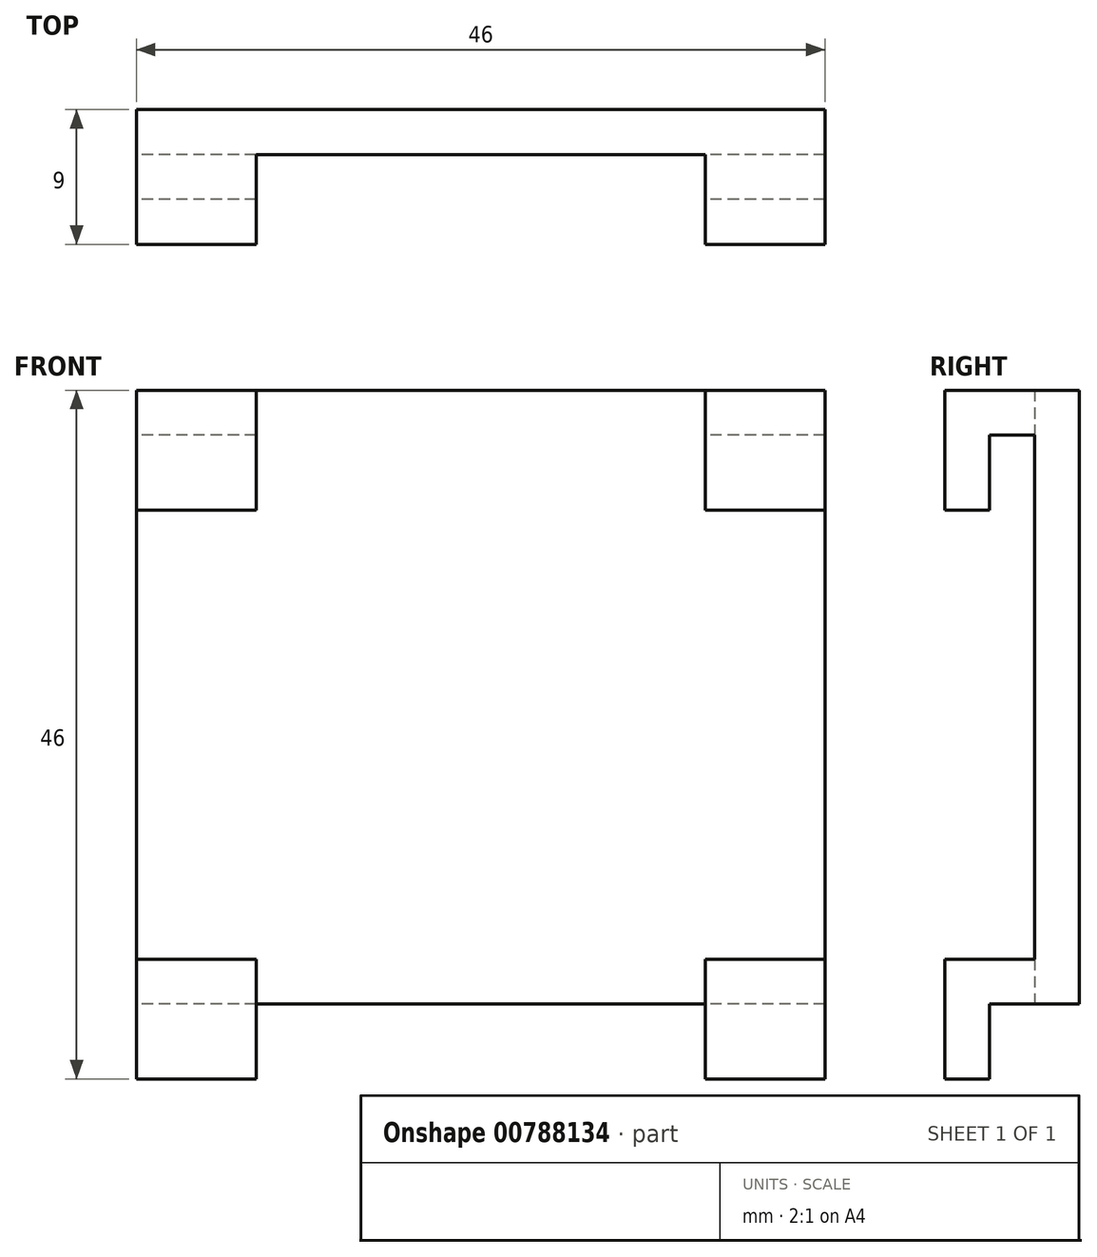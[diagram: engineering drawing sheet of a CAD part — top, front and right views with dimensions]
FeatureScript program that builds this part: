
annotation { "Feature Type Name" : "Feature", "Feature Type Description" : "" }
export const myFeature = defineFeature(function(context is Context, id is Id, definition is map)
    precondition{}
    {
        {
            var Q0;
            Q0=qCreatedBy(makeId("Front.planeOp"),FACE);
            cPlane(context, id + "F0", {"entities" : qUnion([Q0]), "cplaneType" : CPlaneType.OFFSET, "offset" : 3 * mm, "width" : 152.4 * mm, "height" : 152.4 * mm});
        }
        {
            var Q0;
            Q0=qCreatedBy(makeId("Right.planeOp"),FACE);
            var sketch = newSketch(context, id + "F1", { "sketchPlane" : qUnion([Q0])});
            skLineSegment(sketch, "E0", {"start": v(-6, 38) * mm, "end": v(-6, 3) * mm});
            skLineSegment(sketch, "E1", {"start": v(-6, 3) * mm, "end": v(-12, 3) * mm});
            skLineSegment(sketch, "E2", {"start": v(-12, 3) * mm, "end": v(-12, -5) * mm});
            skLineSegment(sketch, "E3", {"start": v(-12, -5) * mm, "end": v(-9, -5) * mm});
            skLineSegment(sketch, "E4", {"start": v(-9, -5) * mm, "end": v(-9, 0) * mm});
            skLineSegment(sketch, "E5", {"start": v(-9, 0) * mm, "end": v(-3, 0) * mm});
            skLineSegment(sketch, "E6", {"start": v(-3, 0) * mm, "end": v(-3, 41) * mm});
            skLineSegment(sketch, "E7", {"start": v(-3, 41) * mm, "end": v(-12, 41) * mm});
            skLineSegment(sketch, "E8", {"start": v(-12, 41) * mm, "end": v(-12, 33) * mm});
            skLineSegment(sketch, "E9", {"start": v(-12, 33) * mm, "end": v(-9, 33) * mm});
            skLineSegment(sketch, "E10", {"start": v(-9, 33) * mm, "end": v(-9, 38) * mm});
            skLineSegment(sketch, "E11", {"start": v(-9, 38) * mm, "end": v(-6, 38) * mm});
            skSolve(sketch);
        }
        {
            var Q0;
            Q0 = qSketchRegion(id + "F1", true);
            extrude(context, id + "F2", {"entities" : qUnion([Q0]), "depth" : 46 * mm, "offsetDistance" : 25 * mm});
        }
        {
            var Q0;
            Q0=makeQuery(id+"F2.opExtrude","SWEPT_FACE",FACE,{"disambiguationData":[OSD([sQuery(id+"F1.wireOp",EDGE,"E0")])]});
            var sketch = newSketch(context, id + "F3", { "sketchPlane" : qUnion([Q0])});
            skLineSegment(sketch, "E12", {"start": v(23, 3) * mm, "end": v(23, 41) * mm, "construction": true});
            skLineSegment(sketch, "E13.bottom", {"start": v(8, 41) * mm, "end": v(38, 41) * mm});
            skLineSegment(sketch, "E13.top", {"start": v(8, -5) * mm, "end": v(38, -5) * mm});
            skLineSegment(sketch, "E13.left", {"start": v(8, 41) * mm, "end": v(8, -5) * mm});
            skLineSegment(sketch, "E13.right", {"start": v(38, 41) * mm, "end": v(38, -5) * mm});
            skSolve(sketch);
        }
        {
            var Q0;
            Q0 = qSketchRegion(id + "F3", true);
            extrude(context, id + "F4", {"entities" : qUnion([Q0]), "operationType" : NewBodyOperationType.REMOVE, "endBound" : BoundingType.THROUGH_ALL, "depth" : 25 * mm, "offsetDistance" : 25 * mm});
        }
    });
